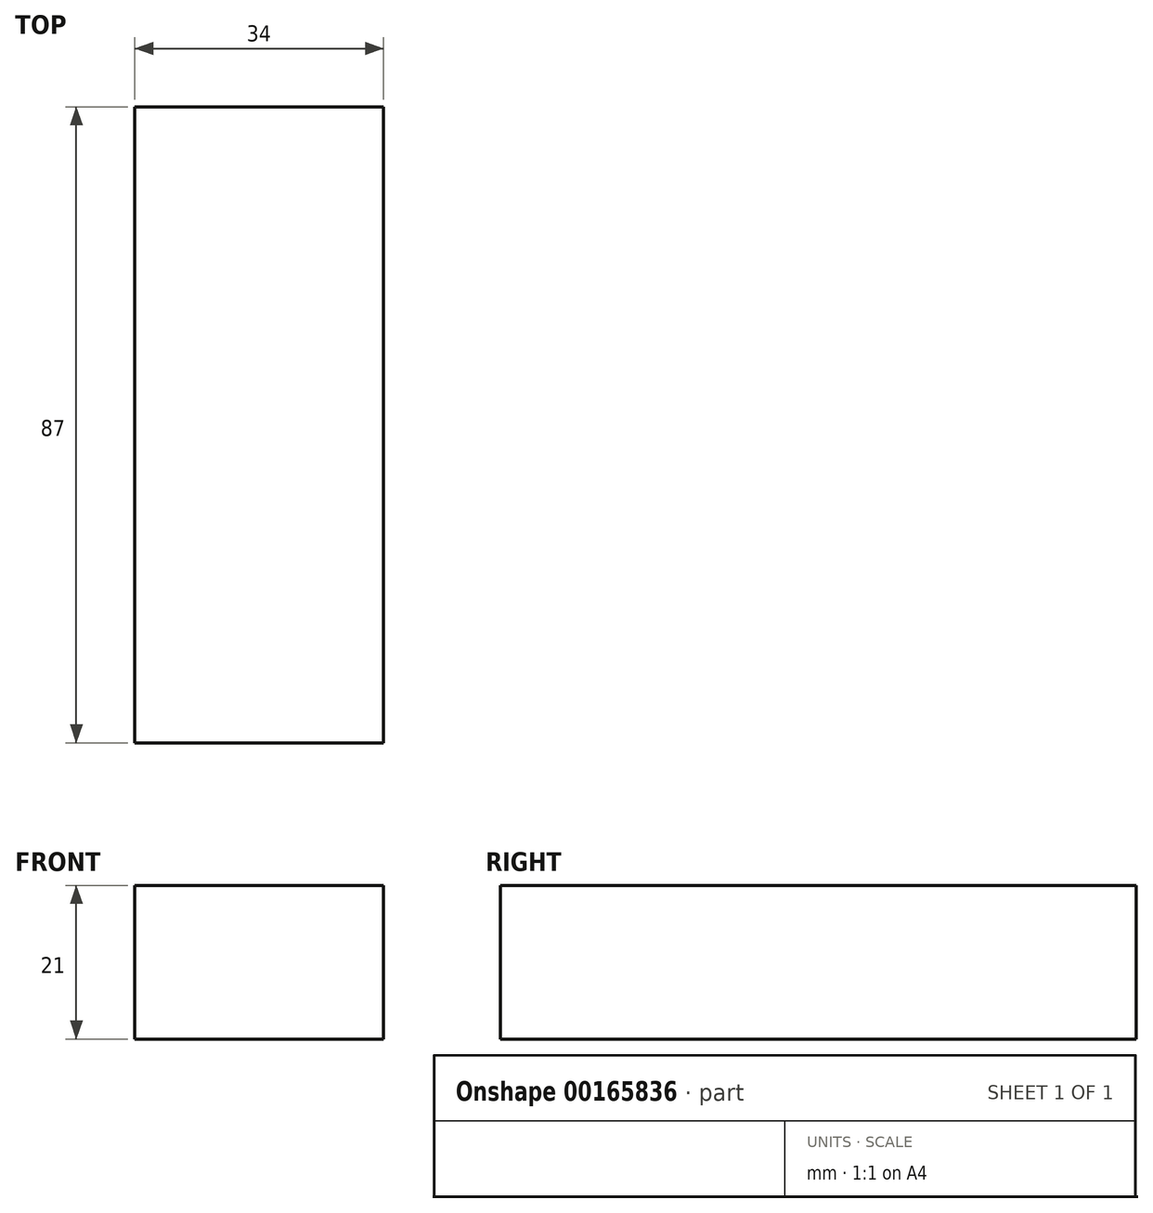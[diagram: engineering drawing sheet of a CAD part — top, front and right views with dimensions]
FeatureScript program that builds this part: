
annotation { "Feature Type Name" : "Feature", "Feature Type Description" : "" }
export const myFeature = defineFeature(function(context is Context, id is Id, definition is map)
    precondition{}
    {
        {
            var Q0;
            Q0=qCreatedBy(makeId("Right.planeOp"),FACE);
            var sketch = newSketch(context, id + "F0", { "sketchPlane" : qUnion([Q0])});
            skLineSegment(sketch, "E0.bottom", {"start": v(43.5, 10.5) * mm, "end": v(-43.5, 10.5) * mm});
            skLineSegment(sketch, "E0.top", {"start": v(43.5, -10.5) * mm, "end": v(-43.5, -10.5) * mm});
            skLineSegment(sketch, "E0.left", {"start": v(43.5, 10.5) * mm, "end": v(43.5, -10.5) * mm});
            skLineSegment(sketch, "E0.right", {"start": v(-43.5, 10.5) * mm, "end": v(-43.5, -10.5) * mm});
            skPoint(sketch, "E0.middle", {"position": v(0, 0) * mm});
            skSolve(sketch);
        }
        {
            var Q0;
            Q0=makeQuery(id+"F0.imprint","IMPRINT",FACE,{"disambiguationData":[TD([[makeQuery(id+"F0.imprint","IMPRINT",EDGE,{"derivedFrom":sQuery(id+"F0.wireOp",EDGE,"E0.bottom")}),1.0]])]});
            extrude(context, id + "F1", {"entities" : qUnion([Q0]), "endBound" : BoundingType.SYMMETRIC, "depth" : 34 * mm});
        }
    });
